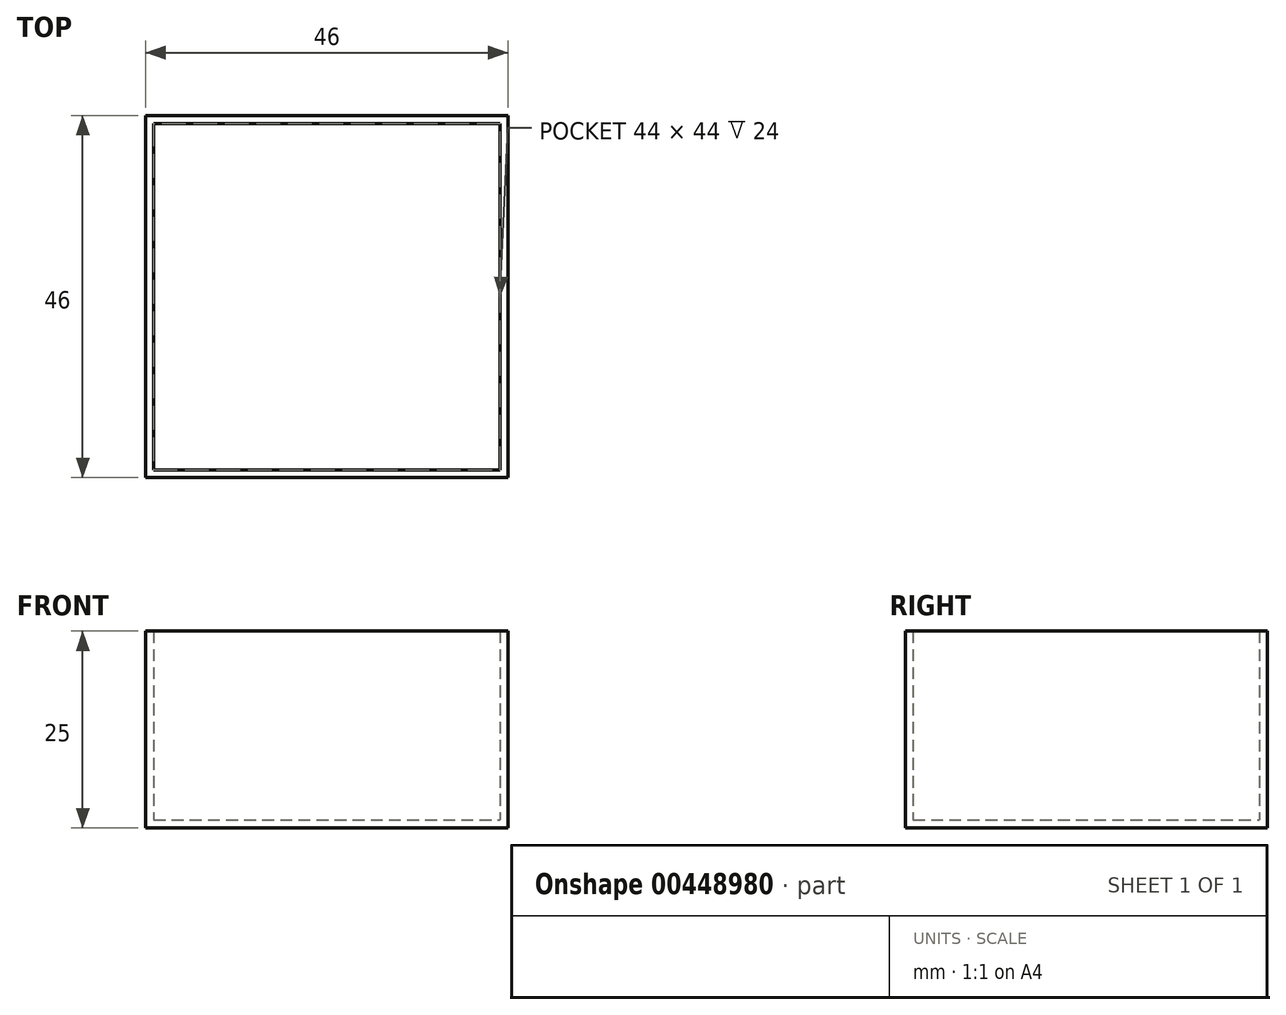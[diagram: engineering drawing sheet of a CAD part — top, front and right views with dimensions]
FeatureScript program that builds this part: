
annotation { "Feature Type Name" : "Feature", "Feature Type Description" : "" }
export const myFeature = defineFeature(function(context is Context, id is Id, definition is map)
    precondition{}
    {
        {
            var Q0;
            Q0=qCreatedBy(makeId("Top.planeOp"),FACE);
            var sketch = newSketch(context, id + "F0", { "sketchPlane" : qUnion([Q0])});
            skLineSegment(sketch, "E0.bottom", {"start": v(0, 0) * mm, "end": v(46, 0) * mm});
            skLineSegment(sketch, "E0.top", {"start": v(0, 46) * mm, "end": v(46, 46) * mm});
            skLineSegment(sketch, "E0.left", {"start": v(0, 0) * mm, "end": v(0, 46) * mm});
            skLineSegment(sketch, "E0.right", {"start": v(46, 0) * mm, "end": v(46, 46) * mm});
            skPoint(sketch, "E1", {"position": v(23, 23) * mm});
            skPoint(sketch, "E1.positionSnap0", {"position": v(23, 0) * mm});
            skPoint(sketch, "E1.positionSnap1", {"position": v(0, 23) * mm});
            skSolve(sketch);
        }
        {
            var Q0;
            Q0 = qSketchRegion(id + "F0", true);
            extrude(context, id + "F1", {"entities" : qUnion([Q0]), "depth" : 25 * mm, "offsetDistance" : 25 * mm});
        }
        {
            var Q0;
            Q0=makeQuery(id+"F1.opExtrude","CAP_FACE",FACE,{"disambiguationData":[OSD([sQuery(id+"F0.wireOp",EDGE,"E0.bottom"),sQuery(id+"F0.wireOp",EDGE,"E0.top"),sQuery(id+"F0.wireOp",EDGE,"E0.left"),sQuery(id+"F0.wireOp",EDGE,"E0.right")])],"isStart":false});
            shell(context, id + "F2", {"entities" : qUnion([Q0]), "thickness" : 1 * mm});
        }
    });
